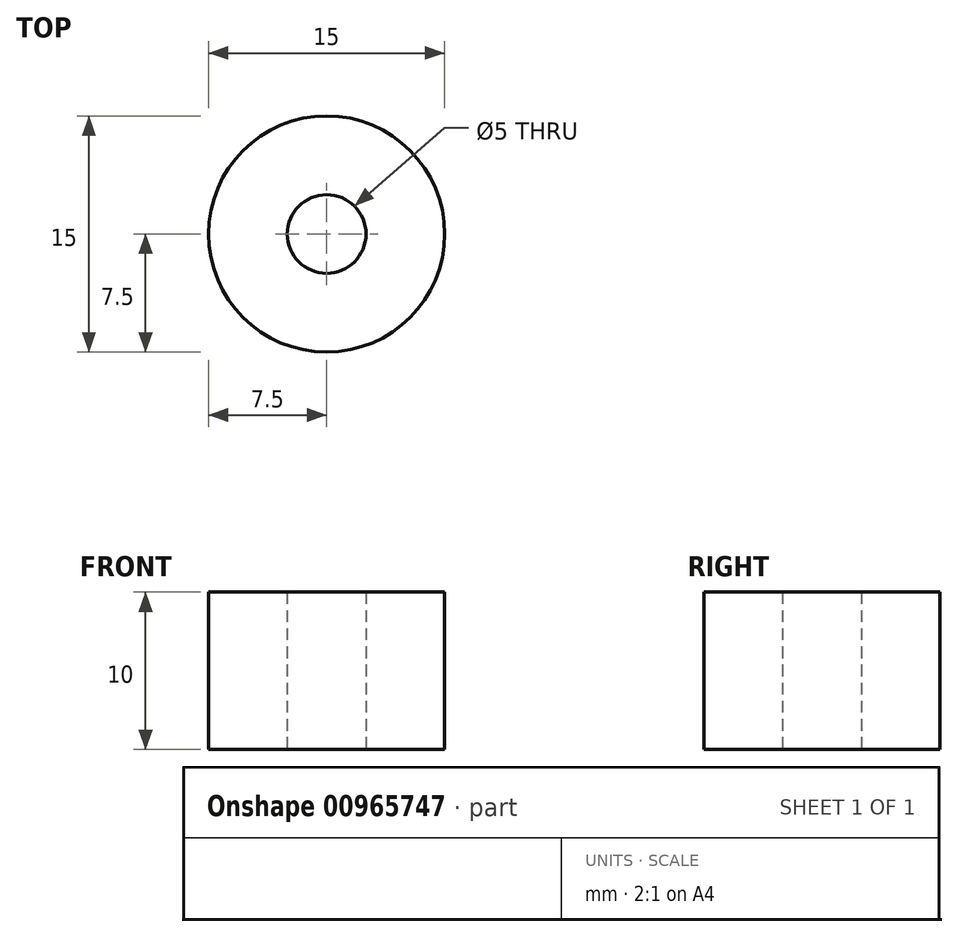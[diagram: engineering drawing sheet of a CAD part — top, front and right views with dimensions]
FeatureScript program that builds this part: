
annotation { "Feature Type Name" : "Feature", "Feature Type Description" : "" }
export const myFeature = defineFeature(function(context is Context, id is Id, definition is map)
    precondition{}
    {
        {
            var Q0;
            Q0=qCreatedBy(makeId("Top.planeOp"),FACE);
            var sketch = newSketch(context, id + "F0", { "sketchPlane" : qUnion([Q0])});
            skCircle(sketch, "E0", {"center": v(0, 0) * mm, "radius": 7.5 * mm});
            skCircle(sketch, "E1", {"center": v(0, 0) * mm, "radius": 2.5 * mm});
            skSolve(sketch);
        }
        {
            var Q0;
            Q0=makeQuery(id+"F0.imprint","IMPRINT",FACE,{"disambiguationData":[TD([[makeQuery(id+"F0.imprint","IMPRINT",EDGE,{"derivedFrom":sQuery(id+"F0.wireOp",EDGE,"E0")}),1.0]])]});
            extrude(context, id + "F1", {"entities" : qUnion([Q0]), "depth" : 10 * mm, "offsetDistance" : 25 * mm});
        }
    });
